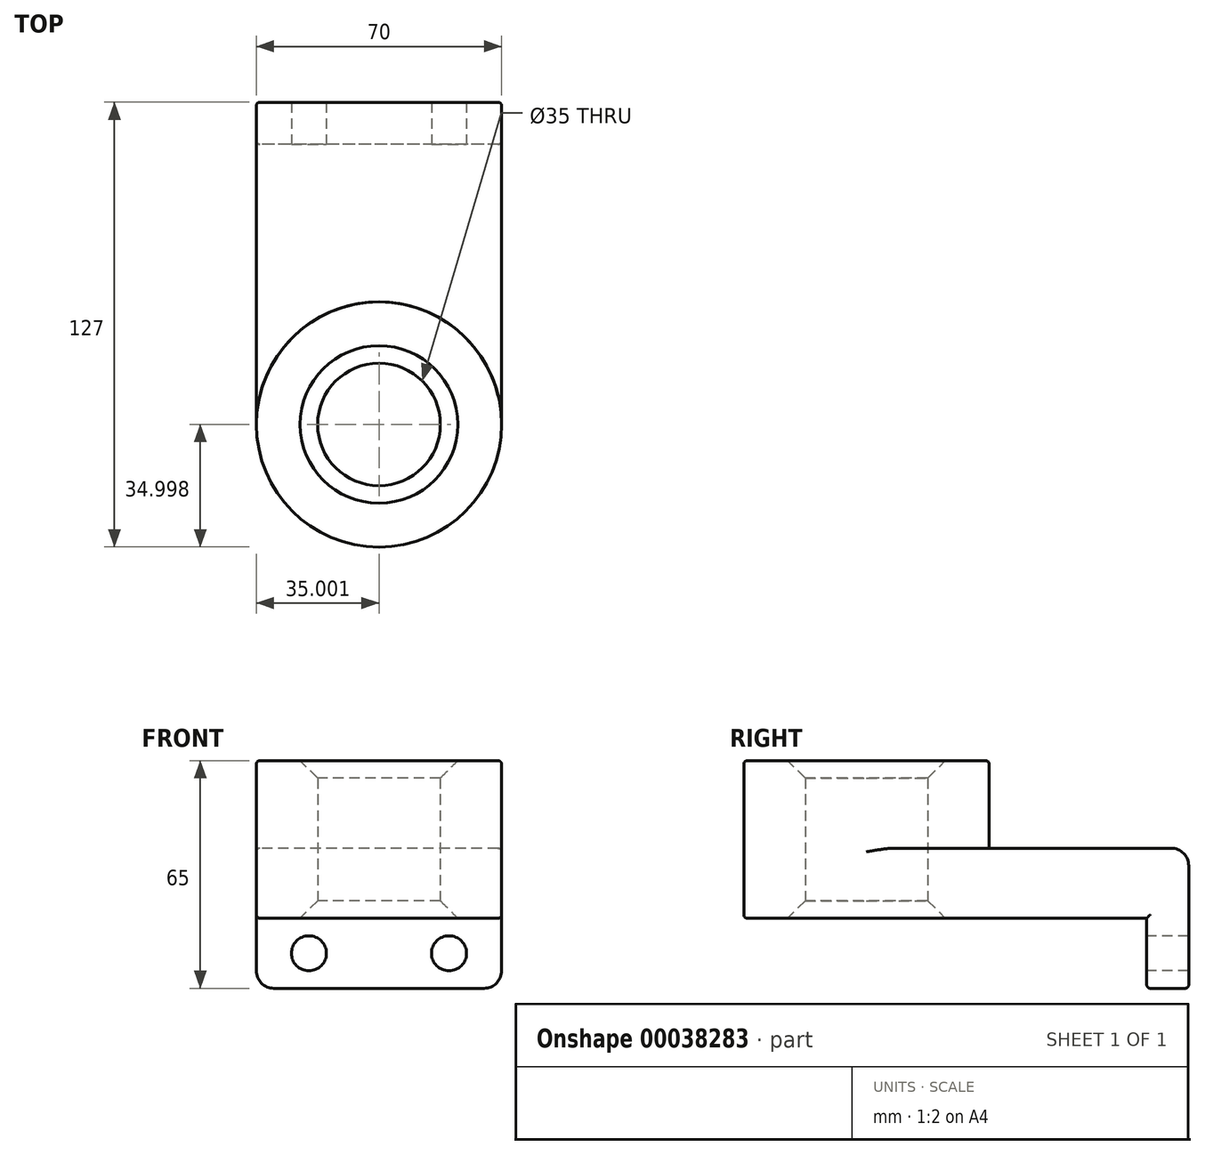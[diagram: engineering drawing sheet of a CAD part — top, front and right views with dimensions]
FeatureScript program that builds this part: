
annotation { "Feature Type Name" : "Feature", "Feature Type Description" : "" }
export const myFeature = defineFeature(function(context is Context, id is Id, definition is map)
    precondition{}
    {
        {
            var Q0;
            Q0=qCreatedBy(makeId("Top.planeOp"),FACE);
            var sketch = newSketch(context, id + "F0", { "sketchPlane" : qUnion([Q0])});
            skCircle(sketch, "E0", {"center": v(-41.2, -49.83) * mm, "radius": 35 * mm});
            skCircle(sketch, "E1", {"center": v(-41.2, -49.83) * mm, "radius": 17.5 * mm});
            skLineSegment(sketch, "E2", {"start": v(-41.2, -49.83) * mm, "end": v(-6.2, -49.83) * mm});
            skLineSegment(sketch, "E3", {"start": v(-41.2, -49.83) * mm, "end": v(-76.2, -49.83) * mm});
            skLineSegment(sketch, "E4", {"start": v(-6.2, -49.83) * mm, "end": v(-6.2, 30.17) * mm});
            skLineSegment(sketch, "E5", {"start": v(-6.2, 30.17) * mm, "end": v(-76.2, 30.17) * mm});
            skLineSegment(sketch, "E6", {"start": v(-76.2, 30.17) * mm, "end": v(-76.2, -49.83) * mm});
            skSolve(sketch);
        }
        {
            var Q0;
            {var subQ1=sQuery(id+"F0.wireOp",EDGE,"E1");var subQ5=sQuery(id+"F0.wireOp",EDGE,"E2");var subQ6=makeQuery(id+"F0.imprint","INTERSECT",VERTEX,{"derivedFrom":[subQ1,subQ5]});Q0=makeQuery(id+"F0.imprint","IMPRINT",FACE,{"disambiguationData":[TD([[makeQuery(id+"F0.imprint","IMPRINT",EDGE,{"disambiguationData":[TD([[subQ6,-1.0]])],"derivedFrom":subQ1}),-1.0]])]});}
            var Q1;
            {var subQ1=sQuery(id+"F0.wireOp",EDGE,"E1");var subQ5=sQuery(id+"F0.wireOp",EDGE,"E2");var subQ6=makeQuery(id+"F0.imprint","INTERSECT",VERTEX,{"derivedFrom":[subQ1,subQ5]});Q1=makeQuery(id+"F0.imprint","IMPRINT",FACE,{"disambiguationData":[TD([[makeQuery(id+"F0.imprint","IMPRINT",EDGE,{"disambiguationData":[TD([[subQ6,1.0]])],"derivedFrom":subQ1}),-1.0]])]});}
            extrude(context, id + "F1", {"entities" : qUnion([Q0, Q1]), "depth" : 45 * mm});
        }
        {
            var Q0;
            Q0 = qSketchRegion(id + "F0", true);
            extrude(context, id + "F2", {"entities" : qUnion([Q0]), "operationType" : NewBodyOperationType.ADD, "depth" : 20 * mm});
        }
        {
            var Q0;
            Q0=makeQuery(id+"F2.opExtrude","SWEPT_FACE",FACE,{"disambiguationData":[OSD([sQuery(id+"F0.wireOp",EDGE,"E5")])]});
            var sketch = newSketch(context, id + "F3", { "sketchPlane" : qUnion([Q0])});
            skLineSegment(sketch, "E7.bottom", {"start": v(6.2, 20) * mm, "end": v(76.2, 20) * mm});
            skLineSegment(sketch, "E7.top", {"start": v(6.2, -20) * mm, "end": v(76.2, -20) * mm});
            skLineSegment(sketch, "E7.left", {"start": v(6.2, 20) * mm, "end": v(6.2, -20) * mm});
            skLineSegment(sketch, "E7.right", {"start": v(76.2, 20) * mm, "end": v(76.2, -20) * mm});
            skCircle(sketch, "E8", {"center": v(21.2, -10) * mm, "radius": 5 * mm});
            skLineSegment(sketch, "E9", {"start": v(21.2, -10) * mm, "end": v(21.2, -5) * mm});
            skLineSegment(sketch, "E10", {"start": v(41.2, -20) * mm, "end": v(41.2, 52.87) * mm, "construction": true});
            skPoint(sketch, "E10.endSnap0", {"position": v(41.2, 20) * mm});
            skCircle(sketch, "E11.MirrorC", {"center": v(61.2, -10) * mm, "radius": 5 * mm});
            skSolve(sketch);
        }
        {
            var Q0;
            {var subQ1=sQuery(id+"F3.wireOp",EDGE,"E7.top");Q0=makeQuery(id+"F3.imprint","IMPRINT",FACE,{"disambiguationData":[TD([[makeQuery(id+"F3.imprint","IMPRINT",EDGE,{"derivedFrom":subQ1}),1.0]])]});}
            var Q1;
            {var subQ2=sQuery(id+"F3.wireOp",EDGE,"E7.bottom");Q1=makeQuery(id+"F3.imprint","IMPRINT",FACE,{"disambiguationData":[TD([[makeQuery(id+"F3.imprint","IMPRINT",EDGE,{"derivedFrom":subQ2}),-1.0]])]});}
            extrude(context, id + "F4", {"entities" : qUnion([Q0, Q1]), "operationType" : NewBodyOperationType.ADD, "depth" : 12 * mm});
        }
        {
            var Q0;
            Q0=makeQuery(id+"F1.opExtrude","CAP_EDGE",EDGE,{"disambiguationData":[OSD([sQuery(id+"F0.wireOp",EDGE,"E1")])],"isStart":false});
            chamfer(context, id + "F5", {"entities" : qUnion([Q0]), "width" : 5 * mm, "tangentPropagation" : true});
        }
        {
            var Q0;
            Q0=makeQuery(id+"F1.opExtrude","CAP_EDGE",EDGE,{"disambiguationData":[OSD([sQuery(id+"F0.wireOp",EDGE,"E1")])],"isStart":true});
            chamfer(context, id + "F6", {"entities" : qUnion([Q0]), "width" : 5 * mm, "tangentPropagation" : true});
        }
        {
            var Q0;
            Q0=makeQuery(id+"F4.opExtrude","SWEPT_EDGE",EDGE,{"disambiguationData":[OSD([sQuery(id+"F3.wireOp",EDGE,"E7.top"),sQuery(id+"F3.wireOp",EDGE,"E7.right")])]});
            var Q1;
            Q1=makeQuery(id+"F4.opExtrude","SWEPT_EDGE",EDGE,{"disambiguationData":[OSD([sQuery(id+"F3.wireOp",EDGE,"E7.top"),sQuery(id+"F3.wireOp",EDGE,"E7.left")])]});
            var Q2;
            Q2=makeQuery(id+"F4.opExtrude","CAP_EDGE",EDGE,{"disambiguationData":[OSD([sQuery(id+"F3.wireOp",EDGE,"E7.bottom")])],"isStart":false});
            fillet(context, id + "F7", {"entities" : qUnion([Q0, Q1, Q2]), "radius" : 5 * mm, "tangentPropagation" : true, "allowEdgeOverflow" : false});
        }
        {
            var Q0;
            Q0=makeQuery(id+"F2.opExtrude","CAP_EDGE",EDGE,{"disambiguationData":[OSD([sQuery(id+"F0.wireOp",EDGE,"E6")])],"isStart":true});
            var Q1;
            Q1=makeQuery(id+"F4.boolean.opBoolean","MERGE",EDGE,{"derivedFrom":[makeQuery(id+"F2.opExtrude","CAP_EDGE",EDGE,{"disambiguationData":[OSD([sQuery(id+"F0.wireOp",EDGE,"E6")])],"isStart":false}),makeQuery(id+"F4.opExtrude","SWEPT_EDGE",EDGE,{"disambiguationData":[OSD([sQuery(id+"F3.wireOp",EDGE,"E7.bottom"),sQuery(id+"F3.wireOp",EDGE,"E7.right")])]})]});
            var Q2;
            Q2=makeQuery(id+"F1.opExtrude","CAP_EDGE",EDGE,{"disambiguationData":[OSD([sQuery(id+"F0.wireOp",EDGE,"E0")])],"isStart":true});
            var Q3;
            Q3=makeQuery(id+"F2.opExtrude","CAP_EDGE",EDGE,{"disambiguationData":[OSD([sQuery(id+"F0.wireOp",EDGE,"E4")])],"isStart":true});
            var Q4;
            Q4=makeQuery(id+"F4.opExtrude","CAP_EDGE",EDGE,{"disambiguationData":[OSD([sQuery(id+"F3.wireOp",EDGE,"E7.top")])],"isStart":true});
            var Q5;
            Q5=makeQuery(id+"F4.boolean.opBoolean","MERGE",EDGE,{"derivedFrom":[makeQuery(id+"F2.opExtrude","CAP_EDGE",EDGE,{"disambiguationData":[OSD([sQuery(id+"F0.wireOp",EDGE,"E4")])],"isStart":false}),makeQuery(id+"F4.opExtrude","SWEPT_EDGE",EDGE,{"disambiguationData":[OSD([sQuery(id+"F3.wireOp",EDGE,"E7.bottom"),sQuery(id+"F3.wireOp",EDGE,"E7.left")])]})]});
            var Q6;
            Q6=makeQuery(id+"F4.opExtrude","CAP_EDGE",EDGE,{"disambiguationData":[OSD([sQuery(id+"F3.wireOp",EDGE,"E7.top")])],"isStart":false});
            var Q7;
            Q7=makeQuery(id+"F4.opExtrude","CAP_EDGE",EDGE,{"disambiguationData":[OSD([sQuery(id+"F3.wireOp",EDGE,"E7.left")])],"isStart":false});
            var Q8;
            Q8=makeQuery(id+"F4.opExtrude","CAP_EDGE",EDGE,{"disambiguationData":[OSD([sQuery(id+"F3.wireOp",EDGE,"E7.right")])],"isStart":false});
            fillet(context, id + "F8", {"entities" : qUnion([Q0, Q1, Q2, Q3, Q4, Q5, Q6, Q7, Q8]), "radius" : 1 * mm, "tangentPropagation" : true, "allowEdgeOverflow" : false});
        }
        {
            var Q0;
            Q0=makeQuery(id+"F1.opExtrude","CAP_EDGE",EDGE,{"disambiguationData":[OSD([sQuery(id+"F0.wireOp",EDGE,"E0")])],"isStart":false});
            fillet(context, id + "F9", {"entities" : qUnion([Q0]), "radius" : 1 * mm, "tangentPropagation" : true, "allowEdgeOverflow" : false});
        }
    });
